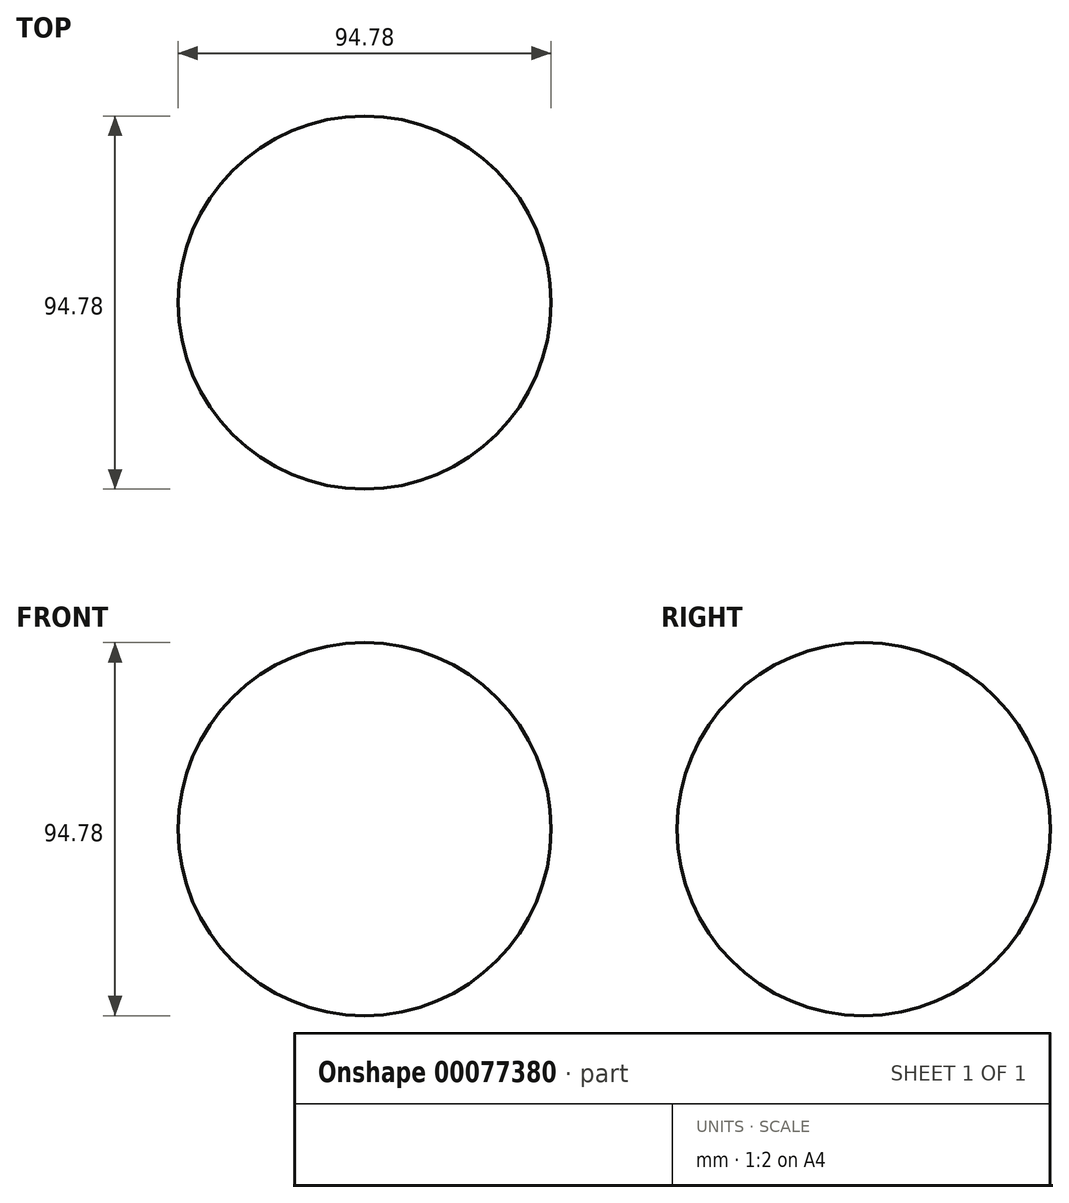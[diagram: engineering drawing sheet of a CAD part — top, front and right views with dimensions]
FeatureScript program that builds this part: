
annotation { "Feature Type Name" : "Feature", "Feature Type Description" : "" }
export const myFeature = defineFeature(function(context is Context, id is Id, definition is map)
    precondition{}
    {
        {
            var Q0;
            Q0=qCreatedBy(makeId("Top.planeOp"),FACE);
            var sketch = newSketch(context, id + "F0", { "sketchPlane" : qUnion([Q0])});
            skArc(sketch, "E0", {"start": v(0, -47.4) * mm, "mid": v(47.4, 0) * mm, "end": v(0, 47.4) * mm});
            skLineSegment(sketch, "E1", {"start": v(0, 47.4) * mm, "end": v(0, -47.4) * mm});
            skPoint(sketch, "E2.orphan", {"position": v(0, 60.3) * mm});
            skSolve(sketch);
        }
        {
            var Q0;
            Q0=makeQuery(id+"F0.imprint","IMPRINT",FACE,{"disambiguationData":[TD([[makeQuery(id+"F0.imprint","IMPRINT",EDGE,{"derivedFrom":sQuery(id+"F0.wireOp",EDGE,"E0")}),1.0]])]});
            var Q1;
            Q1=sQuery(id+"F0.wireOp",EDGE,"E1");
            revolve(context, id + "F1", {"entities" : qUnion([Q0]), "axis" : qUnion([Q1]), "revolveType" : RevolveType.FULL});
        }
    });
